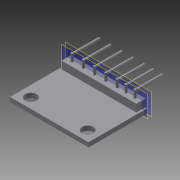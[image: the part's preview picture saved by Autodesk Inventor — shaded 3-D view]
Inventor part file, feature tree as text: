
AUTODESK INVENTOR PART (.ipt)
format: ipt  version: 2015 (Build 190159000, 159)  size: 165,376 bytes
history: native  units: in
note: dims shown in document units (in); Inventor stores cm internally (conversion verified against a paired STEP export)
features: extrude x4, sketch x4, plane x2
ambient origin geometry x8: Origin, YZ Plane, XZ Plane, XY Plane, X Axis, Y Axis, Z Axis, Center Point
bodies: Solid1 (feature_tree)
feature tree (10):
  extrude  "Extrusion1"  Depth=0.622in
  extrude  "Extrusion2"  Depth=0.1181in
  extrude  "Extrusion3"  Depth=0.1142in
  plane  "Work Plane2"
  extrude  "Extrusion4"  Depth=0.2953in
  sketch  "Sketch1"  dims[d0=0.8268in d1=0.622in]
  sketch  "Sketch2"  dims[d2=0.1181in d3=0.1181in]
  sketch  "Sketch3"  dims[d4=0.1142in d5=0.1142in]
  plane  "Work Plane1"
  sketch  "Sketch4"  dims[d6=0.1063in d7=0.1063in d8=0.0472in d9=0.0in d10=0.7874in d11=0.0984in d12=0.0in d13=0.0197in d14=0.0787in d15=0.0in d16=0.0236in d17=0.0236in d18=0.0236in d19=0.0236in d20=0.0236in d21=0.0236in d22=0.0236in d24=0.063in d25=0.1181in d26=0.1181in d27=0.1181in d28=0.1181in d29=0.1181in d30=0.1181in d31=0.0787in d32=0.0in d33=90.0deg d34=-0.0591in d37=0.0236in d38=0.0236in d39=0.0236in d40=0.0236in d41=0.0236in d42=0.0236in d43=0.0236in d44=0.2953in d45=0.0in]
